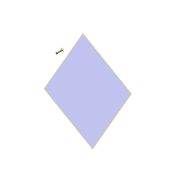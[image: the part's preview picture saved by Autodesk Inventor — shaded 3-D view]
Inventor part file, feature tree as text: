
AUTODESK INVENTOR PART (.ipt)
format: ipt  version: 2016 (Build 200138000, 138)  size: 133,632 bytes
history: native  units: mm
features: sketch x6, extrude x5, plane x2, thread x1, hole x1, chamfer x1
ambient origin geometry x8: Origin, YZ Plane, XZ Plane, XY Plane, X Axis, Y Axis, Z Axis, Center Point
bodies: Solid1 (feature_tree)
feature tree (16):
  plane  "Work Plane1"
  extrude  "Extrusion1"  Depth=36.5mm TaperAngle=0.0deg
  extrude  "Extrusion2"  Depth=4.5mm TaperAngle=0.0deg
  thread  "Thread1"  [1 undecoded]
  plane  "Work Plane2"
  extrude  "Extrusion4"  Depth=1.0mm
  hole  "Hole1"  [1 undecoded]
  extrude  "Extrusion5"  Depth=2.0mm
  extrude  "Extrusion6"  Depth=1.0mm TaperAngle=0.0deg
  chamfer  "Chamfer2"  Distance=0.3mm Angle=45.0deg
  sketch  "Sketch1"  dims[d0=8.0mm d1=36.5mm d2=0.0mm]
  sketch  "Sketch2"  dims[d3=13.0mm d4=4.5mm d5=0.0mm d11=21.0mm d12=0.0mm]
  sketch  "Sketch4"  dims[d16=1.0mm d17=1.0mm]
  sketch  "Sketch5"  dims[d18=0.9mm d19=0.0mm]
  sketch  "Sketch6"  dims[d20=2.459mm d21=8.0mm d22=5.0mm d23=2.0mm d24=90.0deg d25=10.8mm d26=20.594885mm d27=0.2mm d28=0.0mm]
  sketch  "Sketch7"  dims[d29=5.5mm d30=6.8mm d31=1.0mm d32=0.0mm d33=0.3mm d34=2.0mm d35=45.0deg]
note: 2 required parameter values undecoded (feature->parameter linkage not recoverable at this tier; creation-order binding heuristic only, values carry confidence <= 0.55)
